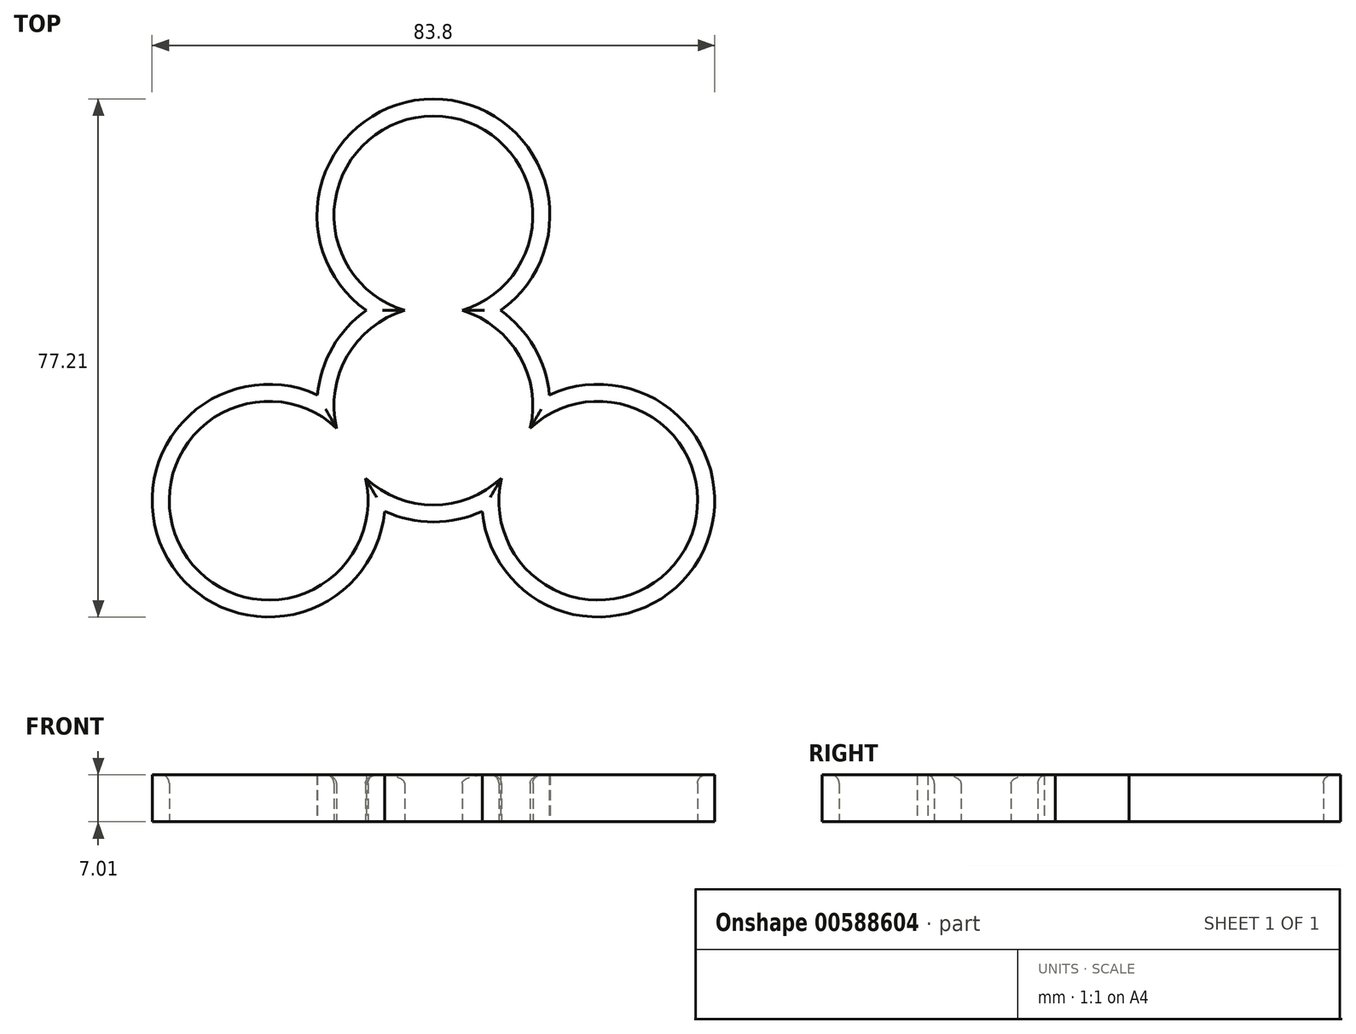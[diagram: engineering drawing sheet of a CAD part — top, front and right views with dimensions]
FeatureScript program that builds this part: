
annotation { "Feature Type Name" : "Feature", "Feature Type Description" : "" }
export const myFeature = defineFeature(function(context is Context, id is Id, definition is map)
    precondition{}
    {
        {
            var Q0;
            Q0=qCreatedBy(makeId("Top.planeOp"),FACE);
            var sketch = newSketch(context, id + "F0", { "sketchPlane" : qUnion([Q0])});
            skCircle(sketch, "E0", {"center": v(0, 0) * mm, "radius": 11 * mm});
            skArc(sketch, "E1.0", {"start": v(-15.1, -8.55) * mm, "mid": v(-15.02, -8.67) * mm, "end": v(-14.95, -8.8) * mm});
            skArc(sketch, "E2", {"start": v(10, 14.17) * mm, "mid": v(0, 45.7) * mm, "end": v(-10, 14.17) * mm});
            skPoint(sketch, "E2.second.point", {"position": v(0, 45.7) * mm});
            skPoint(sketch, "E2.third.point", {"position": v(-10.78, 41.94) * mm});
            skLineSegment(sketch, "E3", {"start": v(0, 17.35) * mm, "end": v(0, 11) * mm, "construction": true});
            skArc(sketch, "E4.1.0", {"start": v(-17.28, 1.58) * mm, "mid": v(-39.57, -22.85) * mm, "end": v(-7.27, -15.75) * mm});
            skArc(sketch, "E4.2.0", {"start": v(7.27, -15.75) * mm, "mid": v(39.57, -22.85) * mm, "end": v(17.28, 1.58) * mm});
            skCircle(sketch, "E5", {"center": v(0, 28.35) * mm, "radius": 11 * mm});
            skCircle(sketch, "E6.1.0", {"center": v(-24.55, -14.17) * mm, "radius": 11 * mm});
            skCircle(sketch, "E6.2.0", {"center": v(24.55, -14.17) * mm, "radius": 11 * mm});
            skPoint(sketch, "E7", {"position": v(-17.28, 1.58) * mm});
            skPoint(sketch, "E8", {"position": v(-7.27, -15.75) * mm});
            skPoint(sketch, "E9", {"position": v(7.27, -15.75) * mm});
            skPoint(sketch, "E10", {"position": v(17.28, 1.58) * mm});
            skPoint(sketch, "E11", {"position": v(10, 14.17) * mm});
            skPoint(sketch, "E12", {"position": v(-10, 14.17) * mm});
            skArc(sketch, "E13.trimOffspring", {"start": v(-7.27, -15.75) * mm, "mid": v(0, -17.35) * mm, "end": v(7.27, -15.75) * mm});
            skArc(sketch, "E14.trimOffspring", {"start": v(-10, 14.17) * mm, "mid": v(-15.02, 8.67) * mm, "end": v(-17.28, 1.58) * mm});
            skArc(sketch, "E15.trimOffspring", {"start": v(0.15, 17.35) * mm, "mid": v(0, 17.35) * mm, "end": v(-0.15, 17.35) * mm});
            skArc(sketch, "E16.trimOffspring", {"start": v(14.95, -8.8) * mm, "mid": v(15.02, -8.67) * mm, "end": v(15.1, -8.55) * mm});
            skArc(sketch, "E17.trimOffspring", {"start": v(17.28, 1.58) * mm, "mid": v(15.02, 8.67) * mm, "end": v(10, 14.17) * mm});
            skSolve(sketch);
        }
        {
            var Q0;
            Q0 = qSketchRegion(id + "F0", true);
            extrude(context, id + "F1", {"entities" : qUnion([Q0]), "depth" : 7 * mm, "offsetDistance" : 25.4 * mm});
        }
        {
            var Q0;
            Q0=makeQuery(id+"F1.opExtrude","CAP_FACE",FACE,{"disambiguationData":[OSD([sQuery(id+"F0.wireOp",EDGE,"E0"),sQuery(id+"F0.wireOp",EDGE,"E2"),sQuery(id+"F0.wireOp",EDGE,"E4.1.0"),sQuery(id+"F0.wireOp",EDGE,"E4.2.0"),sQuery(id+"F0.wireOp",EDGE,"E5"),sQuery(id+"F0.wireOp",EDGE,"E6.1.0"),sQuery(id+"F0.wireOp",EDGE,"E6.2.0"),sQuery(id+"F0.wireOp",EDGE,"E13.trimOffspring"),sQuery(id+"F0.wireOp",EDGE,"E14.trimOffspring"),sQuery(id+"F0.wireOp",EDGE,"E17.trimOffspring")])],"isStart":false});
            var sketch = newSketch(context, id + "F2", { "sketchPlane" : qUnion([Q0])});
            skLineSegment(sketch, "E18", {"start": v(0, 0) * mm, "end": v(0, 14.17) * mm, "construction": true});
            skSolve(sketch);
        }
        {
            var Q0;
            Q0=makeQuery(id+"F1.opExtrude","CAP_FACE",FACE,{"disambiguationData":[OSD([sQuery(id+"F0.wireOp",EDGE,"E0"),sQuery(id+"F0.wireOp",EDGE,"E2"),sQuery(id+"F0.wireOp",EDGE,"E4.1.0"),sQuery(id+"F0.wireOp",EDGE,"E4.2.0"),sQuery(id+"F0.wireOp",EDGE,"E5"),sQuery(id+"F0.wireOp",EDGE,"E6.1.0"),sQuery(id+"F0.wireOp",EDGE,"E6.2.0"),sQuery(id+"F0.wireOp",EDGE,"E13.trimOffspring"),sQuery(id+"F0.wireOp",EDGE,"E14.trimOffspring"),sQuery(id+"F0.wireOp",EDGE,"E17.trimOffspring")])],"isStart":true});
            var sketch = newSketch(context, id + "F3", { "sketchPlane" : qUnion([Q0])});
            skArc(sketch, "E19.0", {"start": v(14.42, 3.37) * mm, "mid": v(12.82, -7.4) * mm, "end": v(4.29, -14.17) * mm});
            skArc(sketch, "E19.1", {"start": v(-4.29, -14.17) * mm, "mid": v(-12.82, -7.4) * mm, "end": v(-14.42, 3.37) * mm});
            skArc(sketch, "E19.2", {"start": v(-14.42, 3.37) * mm, "mid": v(-37.37, 21.58) * mm, "end": v(-10.13, 10.8) * mm});
            skArc(sketch, "E19.3", {"start": v(4.29, -14.17) * mm, "mid": v(0, -43.15) * mm, "end": v(-4.29, -14.17) * mm});
            skArc(sketch, "E19.4", {"start": v(-10.13, 10.8) * mm, "mid": v(0, 14.8) * mm, "end": v(10.13, 10.8) * mm});
            skArc(sketch, "E19.5", {"start": v(10.13, 10.8) * mm, "mid": v(37.37, 21.58) * mm, "end": v(14.42, 3.37) * mm});
            skSolve(sketch);
        }
        {
            var Q0;
            Q0=makeQuery(id+"F3.imprint","IMPRINT",FACE,{"disambiguationData":[TD([[makeQuery(id+"F3.imprint","IMPRINT",EDGE,{"derivedFrom":sQuery(id+"F3.wireOp",EDGE,"E19.0")}),1.0]])]});
            extrude(context, id + "F4", {"entities" : qUnion([Q0]), "operationType" : NewBodyOperationType.REMOVE, "oppositeDirection" : true, "depth" : 25.15 * mm, "offsetDistance" : 25.4 * mm});
        }
        {
            var Q0;
            Q0=makeQuery(id+"F4.boolean.opBoolean","COPY",EDGE,{"derivedFrom":makeQuery(id+"F4.opExtrude","CAP_EDGE",EDGE,{"disambiguationData":[OSD([sQuery(id+"F3.wireOp",EDGE,"E19.4")])],"isStart":true})});
            var Q1;
            Q1=makeQuery(id+"F4.boolean.opBoolean","COPY",EDGE,{"derivedFrom":makeQuery(id+"F4.opExtrude","CAP_EDGE",EDGE,{"disambiguationData":[OSD([sQuery(id+"F3.wireOp",EDGE,"E19.2")])],"isStart":true})});
            var Q2;
            Q2=makeQuery(id+"F4.boolean.opBoolean","COPY",EDGE,{"derivedFrom":makeQuery(id+"F4.opExtrude","CAP_EDGE",EDGE,{"disambiguationData":[OSD([sQuery(id+"F3.wireOp",EDGE,"E19.1")])],"isStart":true})});
            var Q3;
            Q3=makeQuery(id+"F4.boolean.opBoolean","COPY",EDGE,{"derivedFrom":makeQuery(id+"F4.opExtrude","CAP_EDGE",EDGE,{"disambiguationData":[OSD([sQuery(id+"F3.wireOp",EDGE,"E19.3")])],"isStart":true})});
            var Q4;
            Q4=makeQuery(id+"F4.boolean.opBoolean","COPY",EDGE,{"derivedFrom":makeQuery(id+"F4.opExtrude","CAP_EDGE",EDGE,{"disambiguationData":[OSD([sQuery(id+"F3.wireOp",EDGE,"E19.0")])],"isStart":true})});
            var Q5;
            Q5=makeQuery(id+"F4.boolean.opBoolean","COPY",EDGE,{"derivedFrom":makeQuery(id+"F4.opExtrude","CAP_EDGE",EDGE,{"disambiguationData":[OSD([sQuery(id+"F3.wireOp",EDGE,"E19.5")])],"isStart":true})});
            var Q6;
            Q6=makeQuery(id+"F4.boolean.opBoolean","INTERSECT",EDGE,{"derivedFrom":[makeQuery(id+"F1.opExtrude","CAP_FACE",FACE,{"disambiguationData":[OSD([sQuery(id+"F0.wireOp",EDGE,"E0"),sQuery(id+"F0.wireOp",EDGE,"E2"),sQuery(id+"F0.wireOp",EDGE,"E4.1.0"),sQuery(id+"F0.wireOp",EDGE,"E4.2.0"),sQuery(id+"F0.wireOp",EDGE,"E5"),sQuery(id+"F0.wireOp",EDGE,"E6.1.0"),sQuery(id+"F0.wireOp",EDGE,"E6.2.0"),sQuery(id+"F0.wireOp",EDGE,"E13.trimOffspring"),sQuery(id+"F0.wireOp",EDGE,"E14.trimOffspring"),sQuery(id+"F0.wireOp",EDGE,"E17.trimOffspring")])],"isStart":false}),makeQuery(id+"F4.opExtrude","SWEPT_FACE",FACE,{"disambiguationData":[OSD([sQuery(id+"F3.wireOp",EDGE,"E19.4")])]})]});
            var Q7;
            Q7=makeQuery(id+"F4.boolean.opBoolean","INTERSECT",EDGE,{"derivedFrom":[makeQuery(id+"F1.opExtrude","CAP_FACE",FACE,{"disambiguationData":[OSD([sQuery(id+"F0.wireOp",EDGE,"E0"),sQuery(id+"F0.wireOp",EDGE,"E2"),sQuery(id+"F0.wireOp",EDGE,"E4.1.0"),sQuery(id+"F0.wireOp",EDGE,"E4.2.0"),sQuery(id+"F0.wireOp",EDGE,"E5"),sQuery(id+"F0.wireOp",EDGE,"E6.1.0"),sQuery(id+"F0.wireOp",EDGE,"E6.2.0"),sQuery(id+"F0.wireOp",EDGE,"E13.trimOffspring"),sQuery(id+"F0.wireOp",EDGE,"E14.trimOffspring"),sQuery(id+"F0.wireOp",EDGE,"E17.trimOffspring")])],"isStart":false}),makeQuery(id+"F4.opExtrude","SWEPT_FACE",FACE,{"disambiguationData":[OSD([sQuery(id+"F3.wireOp",EDGE,"E19.2")])]})]});
            var Q8;
            Q8=makeQuery(id+"F4.boolean.opBoolean","INTERSECT",EDGE,{"derivedFrom":[makeQuery(id+"F1.opExtrude","CAP_FACE",FACE,{"disambiguationData":[OSD([sQuery(id+"F0.wireOp",EDGE,"E0"),sQuery(id+"F0.wireOp",EDGE,"E2"),sQuery(id+"F0.wireOp",EDGE,"E4.1.0"),sQuery(id+"F0.wireOp",EDGE,"E4.2.0"),sQuery(id+"F0.wireOp",EDGE,"E5"),sQuery(id+"F0.wireOp",EDGE,"E6.1.0"),sQuery(id+"F0.wireOp",EDGE,"E6.2.0"),sQuery(id+"F0.wireOp",EDGE,"E13.trimOffspring"),sQuery(id+"F0.wireOp",EDGE,"E14.trimOffspring"),sQuery(id+"F0.wireOp",EDGE,"E17.trimOffspring")])],"isStart":false}),makeQuery(id+"F4.opExtrude","SWEPT_FACE",FACE,{"disambiguationData":[OSD([sQuery(id+"F3.wireOp",EDGE,"E19.1")])]})]});
            var Q9;
            Q9=makeQuery(id+"F4.boolean.opBoolean","INTERSECT",EDGE,{"derivedFrom":[makeQuery(id+"F1.opExtrude","CAP_FACE",FACE,{"disambiguationData":[OSD([sQuery(id+"F0.wireOp",EDGE,"E0"),sQuery(id+"F0.wireOp",EDGE,"E2"),sQuery(id+"F0.wireOp",EDGE,"E4.1.0"),sQuery(id+"F0.wireOp",EDGE,"E4.2.0"),sQuery(id+"F0.wireOp",EDGE,"E5"),sQuery(id+"F0.wireOp",EDGE,"E6.1.0"),sQuery(id+"F0.wireOp",EDGE,"E6.2.0"),sQuery(id+"F0.wireOp",EDGE,"E13.trimOffspring"),sQuery(id+"F0.wireOp",EDGE,"E14.trimOffspring"),sQuery(id+"F0.wireOp",EDGE,"E17.trimOffspring")])],"isStart":false}),makeQuery(id+"F4.opExtrude","SWEPT_FACE",FACE,{"disambiguationData":[OSD([sQuery(id+"F3.wireOp",EDGE,"E19.3")])]})]});
            var Q10;
            Q10=makeQuery(id+"F4.boolean.opBoolean","INTERSECT",EDGE,{"derivedFrom":[makeQuery(id+"F1.opExtrude","CAP_FACE",FACE,{"disambiguationData":[OSD([sQuery(id+"F0.wireOp",EDGE,"E0"),sQuery(id+"F0.wireOp",EDGE,"E2"),sQuery(id+"F0.wireOp",EDGE,"E4.1.0"),sQuery(id+"F0.wireOp",EDGE,"E4.2.0"),sQuery(id+"F0.wireOp",EDGE,"E5"),sQuery(id+"F0.wireOp",EDGE,"E6.1.0"),sQuery(id+"F0.wireOp",EDGE,"E6.2.0"),sQuery(id+"F0.wireOp",EDGE,"E13.trimOffspring"),sQuery(id+"F0.wireOp",EDGE,"E14.trimOffspring"),sQuery(id+"F0.wireOp",EDGE,"E17.trimOffspring")])],"isStart":false}),makeQuery(id+"F4.opExtrude","SWEPT_FACE",FACE,{"disambiguationData":[OSD([sQuery(id+"F3.wireOp",EDGE,"E19.0")])]})]});
            var Q11;
            Q11=makeQuery(id+"F4.boolean.opBoolean","INTERSECT",EDGE,{"derivedFrom":[makeQuery(id+"F1.opExtrude","CAP_FACE",FACE,{"disambiguationData":[OSD([sQuery(id+"F0.wireOp",EDGE,"E0"),sQuery(id+"F0.wireOp",EDGE,"E2"),sQuery(id+"F0.wireOp",EDGE,"E4.1.0"),sQuery(id+"F0.wireOp",EDGE,"E4.2.0"),sQuery(id+"F0.wireOp",EDGE,"E5"),sQuery(id+"F0.wireOp",EDGE,"E6.1.0"),sQuery(id+"F0.wireOp",EDGE,"E6.2.0"),sQuery(id+"F0.wireOp",EDGE,"E13.trimOffspring"),sQuery(id+"F0.wireOp",EDGE,"E14.trimOffspring"),sQuery(id+"F0.wireOp",EDGE,"E17.trimOffspring")])],"isStart":false}),makeQuery(id+"F4.opExtrude","SWEPT_FACE",FACE,{"disambiguationData":[OSD([sQuery(id+"F3.wireOp",EDGE,"E19.5")])]})]});
            fillet(context, id + "F5", {"entities" : qUnion([Q0, Q1, Q2, Q3, Q4, Q5, Q6, Q7, Q8, Q9, Q10, Q11]), "radius" : 1.27 * mm, "tangentPropagation" : true, "allowEdgeOverflow" : false});
        }
    });
